# Revit family: QF_BOURGEAT_Satellite4G_chaud_1-1_entree325_pleine
name_source: partatom
category: Equipement spécialisé
revit_build: Autodesk Revit 2015 (Build: 20140606_1530(x64)
units: mm (PartAtom-declared; Revit-internal decimal feet)

## types (8) — shared parameters
Certification = NF hygiene alimentaire
Diametre_roue = 160 mm  [stored 0.524934 ft]
Fabricant = BOURGEAT
Fréquence = 50 Hz
Hauteur_roue = 200 mm  [stored 0.656168 ft]
Indice de protection = IP25
Largeur_porte = 500 mm  [stored 1.64042 ft]
Longueur hors tout = 585 mm  [stored 1.91929 ft]
Longueur_poignees_laterales = 688 mm  [stored 2.25722 ft]
Materiau_Poignee_porte = B_Elastomère_TPE_S
Materiau_bac = B_Elastomère_TPE_S
Materiau_bandage = B_Elastomère_TPE_S
Materiau_porte = Acier inoxydable, brossé
Materiau_vitre = Verre, vitrage transparent, trempé
Nature isolant = Mousse sans PU
Phase = 2
Pos_V_IHM = 38 mm  [stored 0.124672 ft]
Profondeur hors tout = 844 mm  [stored 2.76903 ft]
Spécification du Fabricant = Satellite 4G
Tension = 230 V
URL = http://www.bourgeat.fr

## per-type parameters (varying)
| type | Charge max | Consommation énergétique | Hauteur hors tout | Hauteur_poignee_porte_sol | Hauteur_poignees_laterales | Hauteur_porte | Humidification | Intensité nominale | Modèle | Poids net à vide | Poignee_droite | Poignee_gauche | Puissance électrique  |
| GN10_humidification_porte_inox_tirant_gauche | 100.00 kg | 0.4Kw/h NFD40-016 | 1079 mm  [stored 3.54003 ft] | 372 mm  [stored 1.22047 ft] | 757 mm | 832 mm  [stored 2.72966 ft] | Oui | 4 A | 843310 | 55.00 kg | Non | Oui | 950 W |
| GN10_humidification_porte_inox_tirant_droit | 100.00 kg | 0.4Kw/h NFD40-016 | 1079 mm  [stored 3.54003 ft] | 372 mm  [stored 1.22047 ft] | 757 mm | 832 mm  [stored 2.72966 ft] | Oui | 4 A | 843310 + 844000 | 55.00 kg | Oui | Non | 950 W |
| GN10_sans_humidification_porte_inox_tirant_gauche | 100.00 kg | 0.4Kw/h NFD40-016 | 1079 mm  [stored 3.54003 ft] | 372 mm  [stored 1.22047 ft] | 757 mm | 832 mm  [stored 2.72966 ft] | Non | 4 A | 843210 | 55.00 kg | Non | Oui | 950 W |
| GN10_sans_humidification_porte_inox_tirant_droit | 100.00 kg | 0.4Kw/h NFD40-016 | 1079 mm  [stored 3.54003 ft] | 372 mm  [stored 1.22047 ft] | 757 mm | 832 mm  [stored 2.72966 ft] | Non | 4 A | 843210 + 844000 | 55.00 kg | Oui | Non | 950 W |
| GN17_humidification_porte_inox_tirant_droit | 170.00 kg | 0.77Kw/h NFD40-016 | 1575 mm  [stored 5.16732 ft] | 545 mm  [stored 1.78806 ft] | 937 mm  [stored 3.07415 ft] | 1328 mm  [stored 4.35696 ft] | Oui | 8 A | 840317 + 844000 | 90.00 kg | Oui | Non | 1750 W |
| GN17_humidification_porte_inox_tirant_gauche | 170.00 kg | 0.77Kw/h NFD40-016 | 1575 mm  [stored 5.16732 ft] | 545 mm  [stored 1.78806 ft] | 937 mm  [stored 3.07415 ft] | 1328 mm  [stored 4.35696 ft] | Oui | 8 A | 840317 | 90.00 kg | Non | Oui | 1750 W |
| GN17_sans_humidification_porte_inox_tirant_droit | 170.00 kg | 0.77Kw/h NFD40-016 | 1575 mm  [stored 5.16732 ft] | 545 mm  [stored 1.78806 ft] | 937 mm  [stored 3.07415 ft] | 1328 mm  [stored 4.35696 ft] | Non | 8 A | 840217 + 844000 | 90.00 kg | Oui | Non | 1750 W |
| GN17_sans_humidification_porte_inox_tirant_gauche | 170.00 kg | 0.77Kw/h NFD40-016 | 1575 mm  [stored 5.16732 ft] | 545 mm  [stored 1.78806 ft] | 937 mm  [stored 3.07415 ft] | 1328 mm  [stored 4.35696 ft] | Oui | 8 A | 840217 | 90.00 kg | Non | Oui | 1750 W |

note: [stored X ft] marks values corroborated as IEEE doubles in the binary element streams (Revit-internal decimal feet)
